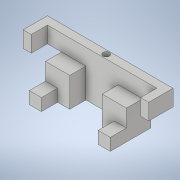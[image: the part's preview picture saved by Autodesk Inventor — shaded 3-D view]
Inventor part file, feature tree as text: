
AUTODESK INVENTOR PART (.ipt)
format: ipt  version: 2020 (Build 240168000, 168)  size: 157,184 bytes
history: native  units: in
note: dims shown in document units (in); Inventor stores cm internally (conversion verified against a paired STEP export)
features: sketch x5, extrude x4, hole x1
ambient origin geometry x8: Origin, YZ Plane, XZ Plane, XY Plane, X Axis, Y Axis, Z Axis, Center Point
bodies: Solid1 (feature_tree)
feature tree (10):
  extrude  "Extrusion1"  Depth=3.875in
  extrude  "Extrusion4"  Depth=0.5in
  extrude  "Extrusion5"  Depth=0.75in
  hole  "Hole2"  [1 undecoded]
  extrude  "Extrusion6"  Depth=0.75in
  sketch  "Sketch1"  dims[d3=0.0in d29=3.875in]
  sketch  "Sketch6"  dims[d30=1.5in d31=0.5in]
  sketch  "Sketch7"  dims[d33=1.0in d34=0.0in d35=0.75in]
  sketch  "Sketch8"  dims[d37=1.0in d38=0.0in d39=0.25in]
  sketch  "Sketch9"  dims[d40=0.397in d41=0.75in d42=0.762in d43=0.25in d44=0.5635in d45=1.0in d46=0.8108in d47=0.75in d48=0.75in d49=0.75in d52=1.0in d53=0.0in d54=0.5in d55=0.0344in d56=0.5in d57=0.0344in]
note: 1 required parameter value undecoded (feature->parameter linkage not recoverable at this tier; creation-order binding heuristic only, values carry confidence <= 0.55)
